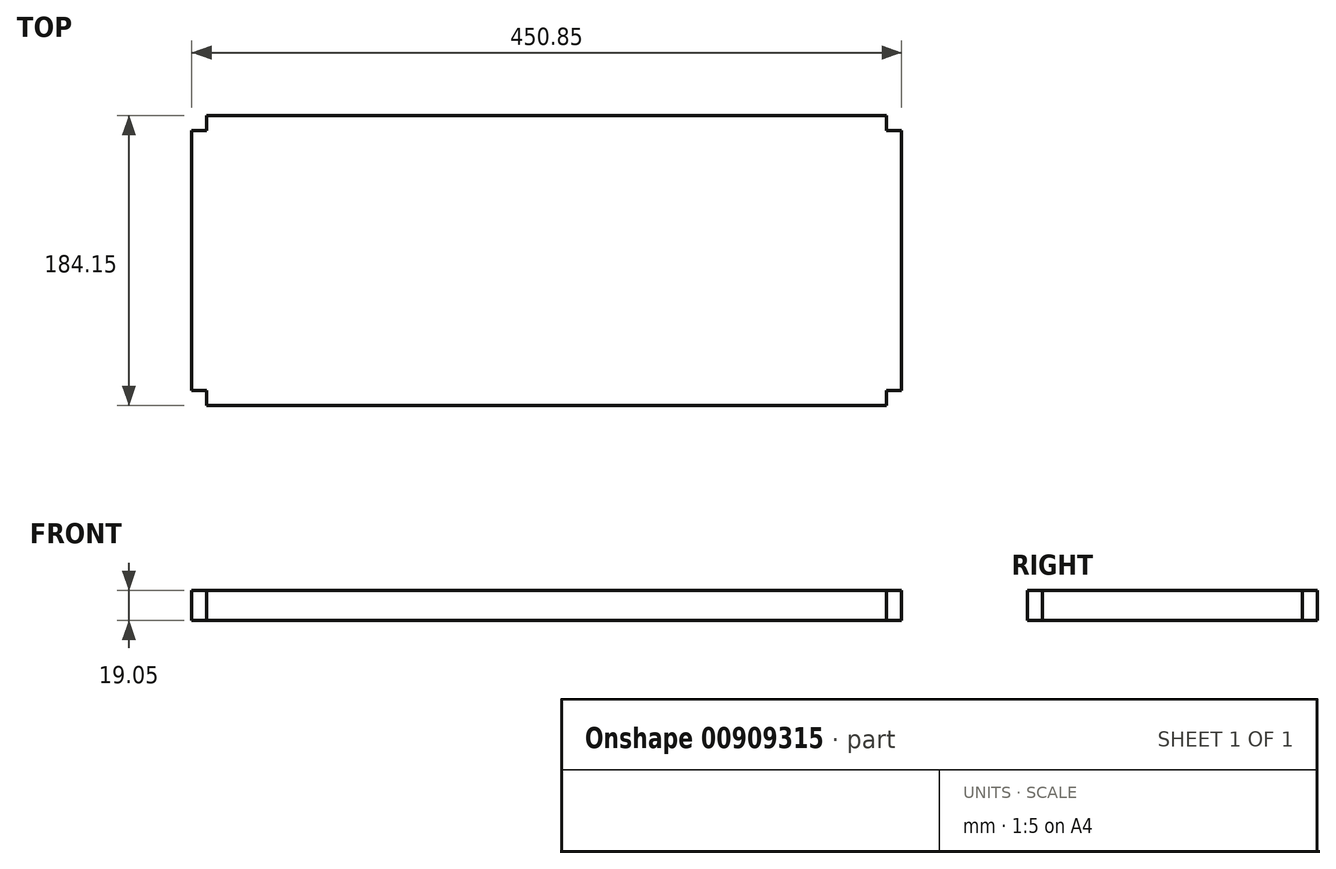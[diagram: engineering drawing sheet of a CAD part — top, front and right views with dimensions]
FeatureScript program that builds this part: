
annotation { "Feature Type Name" : "Feature", "Feature Type Description" : "" }
export const myFeature = defineFeature(function(context is Context, id is Id, definition is map)
    precondition{}
    {
        {
            var Q0;
            Q0=qCreatedBy(makeId("Top.planeOp"),FACE);
            var sketch = newSketch(context, id + "F0", { "sketchPlane" : qUnion([Q0])});
            skLineSegment(sketch, "E0.bottom", {"start": v(0, 0) * mm, "end": v(450.85, 0) * mm});
            skLineSegment(sketch, "E0.top", {"start": v(0, 184.15) * mm, "end": v(450.85, 184.15) * mm});
            skLineSegment(sketch, "E0.left", {"start": v(0, 0) * mm, "end": v(0, 184.15) * mm});
            skLineSegment(sketch, "E0.right", {"start": v(450.85, 0) * mm, "end": v(450.85, 184.15) * mm});
            skSolve(sketch);
        }
        {
            var Q0;
            Q0=makeQuery(id+"F0.imprint","IMPRINT",FACE,{"disambiguationData":[TD([[makeQuery(id+"F0.imprint","IMPRINT",EDGE,{"derivedFrom":sQuery(id+"F0.wireOp",EDGE,"E0.bottom")}),1.0]])]});
            var sketch = newSketch(context, id + "F1", { "sketchPlane" : qUnion([Q0])});
            skLineSegment(sketch, "E1.bottom", {"start": v(0, 0) * mm, "end": v(9.53, 0) * mm});
            skLineSegment(sketch, "E1.top", {"start": v(0, 9.53) * mm, "end": v(9.52, 9.53) * mm});
            skLineSegment(sketch, "E1.left", {"start": v(0, 0) * mm, "end": v(0, 9.53) * mm});
            skLineSegment(sketch, "E1.right", {"start": v(9.53, 0) * mm, "end": v(9.52, 9.53) * mm});
            skLineSegment(sketch, "E2", {"start": v(0, 184.17) * mm, "end": v(0, 174.65) * mm});
            skLineSegment(sketch, "E3", {"start": v(0, 174.65) * mm, "end": v(9.53, 174.65) * mm});
            skLineSegment(sketch, "E4", {"start": v(9.53, 174.65) * mm, "end": v(9.53, 184.17) * mm});
            skLineSegment(sketch, "E5", {"start": v(9.53, 184.17) * mm, "end": v(0, 184.17) * mm});
            skLineSegment(sketch, "E6.MirrorCS", {"start": v(450.85, 0) * mm, "end": v(450.85, 9.53) * mm});
            skLineSegment(sketch, "E7.MirrorCS", {"start": v(450.85, 9.53) * mm, "end": v(441.33, 9.53) * mm});
            skLineSegment(sketch, "E8.MirrorCS", {"start": v(441.33, 0) * mm, "end": v(441.33, 9.53) * mm});
            skLineSegment(sketch, "E9.MirrorCS", {"start": v(441.33, 184.17) * mm, "end": v(450.85, 184.17) * mm});
            skLineSegment(sketch, "E10.MirrorCS", {"start": v(450.85, 184.17) * mm, "end": v(450.85, 174.65) * mm});
            skLineSegment(sketch, "E11.MirrorCS", {"start": v(450.85, 174.65) * mm, "end": v(441.33, 174.65) * mm});
            skLineSegment(sketch, "E12.MirrorCS", {"start": v(441.33, 174.65) * mm, "end": v(441.33, 184.17) * mm});
            skLineSegment(sketch, "E13", {"start": v(441.33, 0) * mm, "end": v(450.85, 0) * mm});
            skSolve(sketch);
        }
        {
            var Q0;
            Q0=makeQuery(id+"F0.imprint","IMPRINT",FACE,{"disambiguationData":[TD([[makeQuery(id+"F0.imprint","IMPRINT",EDGE,{"derivedFrom":sQuery(id+"F0.wireOp",EDGE,"E0.bottom")}),1.0]])]});
            extrude(context, id + "F2", {"entities" : qUnion([Q0]), "depth" : 19.05 * mm, "offsetDistance" : 25.4 * mm});
        }
        {
            var Q0;
            Q0 = qSketchRegion(id + "F1", true);
            extrude(context, id + "F3", {"entities" : qUnion([Q0]), "operationType" : NewBodyOperationType.REMOVE, "depth" : 25.4 * mm, "offsetDistance" : 25.4 * mm});
        }
    });
